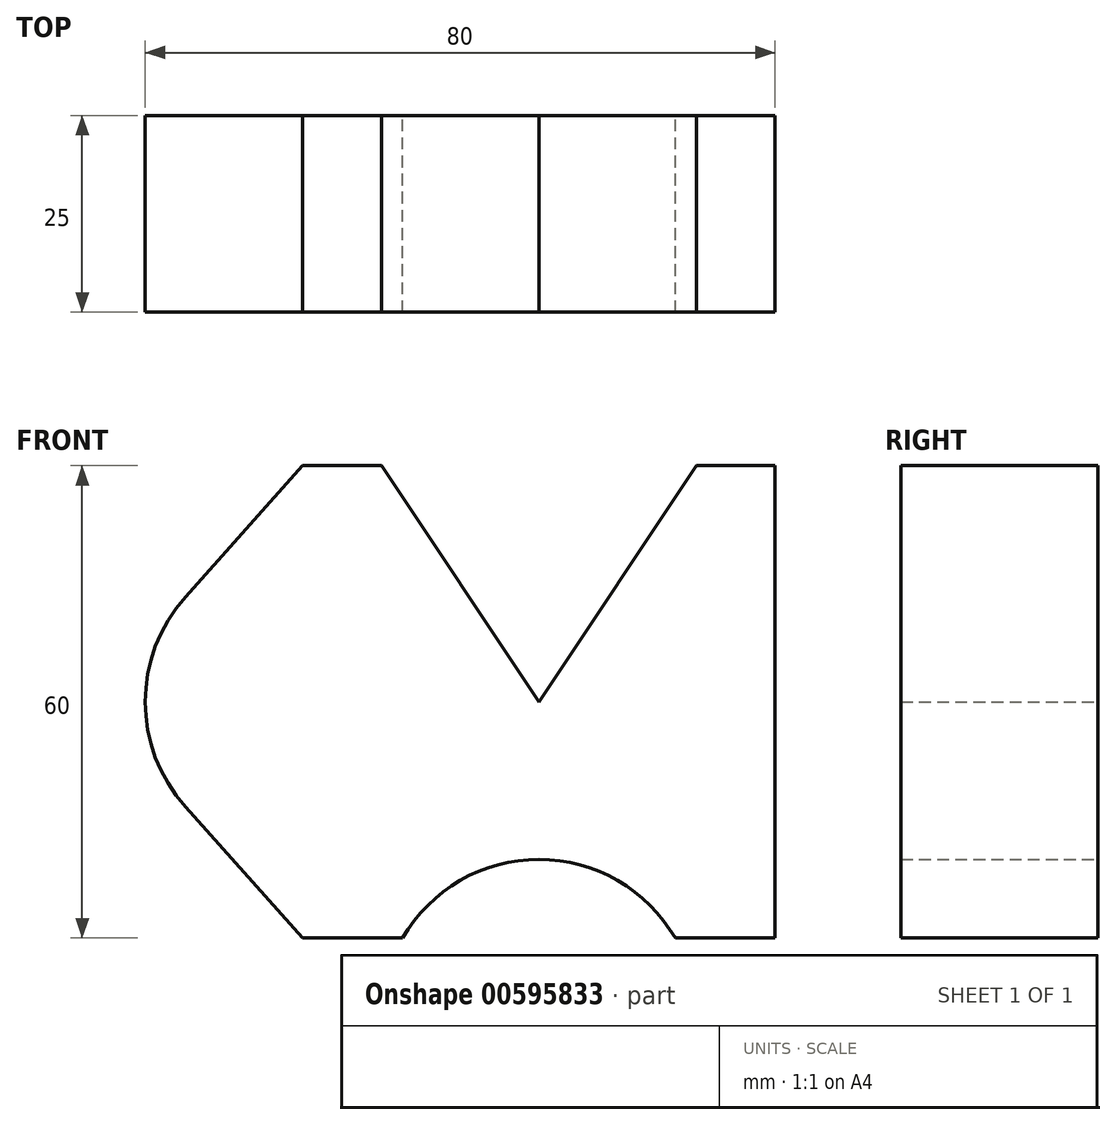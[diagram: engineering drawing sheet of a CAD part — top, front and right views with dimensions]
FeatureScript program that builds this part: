
annotation { "Feature Type Name" : "Feature", "Feature Type Description" : "" }
export const myFeature = defineFeature(function(context is Context, id is Id, definition is map)
    precondition{}
    {
        {
            var Q0;
            Q0=qCreatedBy(makeId("Front.planeOp"),FACE);
            var sketch = newSketch(context, id + "F0", { "sketchPlane" : qUnion([Q0])});
            skLineSegment(sketch, "E0", {"start": v(0, 0) * mm, "end": v(20, 30) * mm});
            skLineSegment(sketch, "E1", {"start": v(20, 30) * mm, "end": v(30, 30) * mm});
            skLineSegment(sketch, "E2", {"start": v(30, 30) * mm, "end": v(30, -30) * mm});
            skLineSegment(sketch, "E3", {"start": v(30, -30) * mm, "end": v(17.32, -30) * mm});
            skArc(sketch, "E4", {"start": v(17.32, -30) * mm, "mid": v(0, -20) * mm, "end": v(-17.32, -30) * mm});
            skLineSegment(sketch, "E5", {"start": v(-17.32, -30) * mm, "end": v(-30, -30) * mm});
            skLineSegment(sketch, "E6", {"start": v(-30, -30) * mm, "end": v(-44.9, -13.33) * mm});
            skLineSegment(sketch, "E7", {"start": v(0, 0) * mm, "end": v(-20, 30) * mm});
            skLineSegment(sketch, "E8", {"start": v(-20, 30) * mm, "end": v(-30, 30) * mm});
            skLineSegment(sketch, "E9", {"start": v(-30, 30) * mm, "end": v(-44.9, 13.33) * mm});
            skArc(sketch, "E10", {"start": v(-44.9, 13.33) * mm, "mid": v(-50, 0) * mm, "end": v(-44.9, -13.33) * mm});
            skLineSegment(sketch, "E11", {"start": v(-30, 30) * mm, "end": v(-30, -30) * mm, "construction": true});
            skSolve(sketch);
        }
        {
            var Q0;
            Q0 = qSketchRegion(id + "F0", true);
            extrude(context, id + "F1", {"entities" : qUnion([Q0]), "depth" : 25 * mm, "offsetDistance" : 25 * mm});
        }
    });
